# Revit family: 307_c7f183209db04ccca2590cd4445be8
name_source: partatom
category: Pipe Accessories
units: mm (PartAtom-declared; Revit-internal decimal feet)

## family parameters
Always vertical = Yes
Cut with Voids When Loaded = No
Part Type = Breaks Into
Round Connector Dimension = Use Diameter
Shared = No
Work Plane-Based = No

## types (5) — shared parameters
CenSd_R12_6 = 10 mm  [stored 0.0328084 ft]
Description = Dirt separator with magnetic inserts, drain valve, F-F conn.
L16 = 14 mm  [stored 0.0459318 ft]
L20 = 14 mm  [stored 0.0459318 ft]
L22 = 2 mm  [stored 0.00656168 ft]
L22__ve = -2 mm  [stored -0.00656168 ft]
L2D = 109 mm
L2D_Min = 3048 mm
L3 = 3 mm  [stored 0.00984252 ft]
L4 = 4 mm  [stored 0.0131234 ft]
L5 = 5 mm  [stored 0.0164042 ft]
L6 = 6 mm  [stored 0.019685 ft]
L8 = 8 mm  [stored 0.0262467 ft]
Manufacturer = FAR
QmdConnectorList = 301;D;302;D
R12 = 12 mm  [stored 0.0393701 ft]
R9 = 12 mm  [stored 0.0393701 ft]
W2D = 25 mm  [stored 0.082021 ft]
magiPartTypeId = 307
magiProductFamilyId = c7f183209db04ccca2590cd4445be8

## per-type parameters (varying)
- 2205 1: A=174 mm; A34=117 mm; BB=10 mm  [stored 0.0328084 ft]; BNTL=59 mm; CenSd_R3_6=16 mm  [stored 0.0524934 ft]; CenSd_R6_6=9 mm  [stored 0.0295276 ft]; D=25 mm; HH=31 mm; HH2=58 mm; L2=55 mm; LL=17 mm; LNT=94 mm; LNT__ve=-94 mm; LR=12 mm  [stored 0.0393701 ft]; LR__ve=-12 mm  [stored -0.0393701 ft]; NT=7 mm  [stored 0.0229659 ft]; NT__ve=-7 mm; R=13 mm; R1=44 mm; R2=40 mm; R22=25 mm  [stored 0.082021 ft]; R3=19 mm; R4=15 mm  [stored 0.0492126 ft]; R5=11 mm  [stored 0.0360892 ft]; R6=10 mm  [stored 0.0328084 ft]; R7=43 mm; R77=42 mm; R77C=37 mm; R77S=21 mm; R8=8 mm  [stored 0.0262467 ft]; magiProductId=b24b66817fbb4e599b3169297f0ace
- 2205 112: A=188 mm; A34=127 mm; BB=12 mm  [stored 0.0393701 ft]; BNTL=64 mm; CenSd_R3_6=23 mm; CenSd_R6_6=9 mm  [stored 0.0295276 ft]; D=40 mm; HH=33 mm; HH2=63 mm; L2=60 mm; LL=21 mm; LNT=103 mm; LNT__ve=-103 mm; LR=13 mm; LR__ve=-13 mm; NT=8 mm  [stored 0.0262467 ft]; NT__ve=-8 mm  [stored -0.0262467 ft]; R=20 mm  [stored 0.0656168 ft]; R1=48 mm; R2=44 mm; R22=27 mm; R3=26 mm; R4=22 mm  [stored 0.0721785 ft]; R5=12 mm  [stored 0.0393701 ft]; R6=11 mm  [stored 0.0360892 ft]; R7=47 mm; R77=46 mm; R77C=40 mm; R77S=23 mm; R8=9 mm  [stored 0.0295276 ft]; magiProductId=3962f5c2ffc24ff3bb7c51e0174143
- 2205 114: A=188 mm; A34=127 mm; BB=12 mm  [stored 0.0393701 ft]; BNTL=64 mm; CenSd_R3_6=19 mm; CenSd_R6_6=9 mm  [stored 0.0295276 ft]; D=32 mm; HH=33 mm; HH2=63 mm; L2=60 mm; LL=21 mm; LNT=103 mm; LNT__ve=-103 mm; LR=13 mm; LR__ve=-13 mm; NT=8 mm  [stored 0.0262467 ft]; NT__ve=-8 mm  [stored -0.0262467 ft]; R=16 mm  [stored 0.0524934 ft]; R1=48 mm; R2=44 mm; R22=27 mm; R3=22 mm  [stored 0.0721785 ft]; R4=18 mm; R5=12 mm  [stored 0.0393701 ft]; R6=11 mm  [stored 0.0360892 ft]; R7=47 mm; R77=46 mm; R77C=40 mm; R77S=23 mm; R8=9 mm  [stored 0.0295276 ft]; magiProductId=74f661cc48a0475ea4063781007844
- 2205 2: A=184 mm; A34=124 mm; BB=15 mm  [stored 0.0492126 ft]; BNTL=63 mm; CenSd_R3_6=27 mm; CenSd_R6_6=10 mm  [stored 0.0328084 ft]; D=50 mm; HH=36 mm; HH2=61 mm; L2=63 mm; LL=20 mm  [stored 0.0656168 ft]; LNT=109 mm; LNT__ve=-109 mm; LR=14 mm  [stored 0.0459318 ft]; LR__ve=-14 mm; NT=8 mm  [stored 0.0262467 ft]; NT__ve=-8 mm  [stored -0.0262467 ft]; R=25 mm  [stored 0.082021 ft]; R1=50 mm; R2=46 mm; R22=28 mm; R3=31 mm; R4=27 mm; R5=13 mm; R6=12 mm  [stored 0.0393701 ft]; R7=50 mm; R77=49 mm; R77C=42 mm; R77S=24 mm  [stored 0.0787402 ft]; R8=10 mm  [stored 0.0328084 ft]; magiProductId=535720fa7c994ee38715db12bd846f
- 2205 34: A=174 mm; A34=117 mm; BB=10 mm  [stored 0.0328084 ft]; BNTL=59 mm; CenSd_R3_6=14 mm  [stored 0.0459318 ft]; CenSd_R6_6=9 mm  [stored 0.0295276 ft]; D=20 mm; HH=31 mm; HH2=58 mm; L2=55 mm; LL=17 mm; LNT=94 mm; LNT__ve=-94 mm; LR=12 mm  [stored 0.0393701 ft]; LR__ve=-12 mm  [stored -0.0393701 ft]; NT=7 mm  [stored 0.0229659 ft]; NT__ve=-7 mm; R=10 mm  [stored 0.0328084 ft]; R1=44 mm; R2=40 mm; R22=25 mm  [stored 0.082021 ft]; R3=16 mm  [stored 0.0524934 ft]; R4=12 mm  [stored 0.0393701 ft]; R5=11 mm  [stored 0.0360892 ft]; R6=10 mm  [stored 0.0328084 ft]; R7=43 mm; R77=42 mm; R77C=37 mm; R77S=21 mm; R8=8 mm  [stored 0.0262467 ft]; magiProductId=d332435fb81c4154ae931f172fefda

note: column(s) folded — value = type name in every type: MC Product Code

note: [stored X ft] marks values corroborated as IEEE doubles in the binary element streams (Revit-internal decimal feet)

## geometry (parser evidence)
native form markers: Sweep x2
no freeform markers — native parametric forms only
